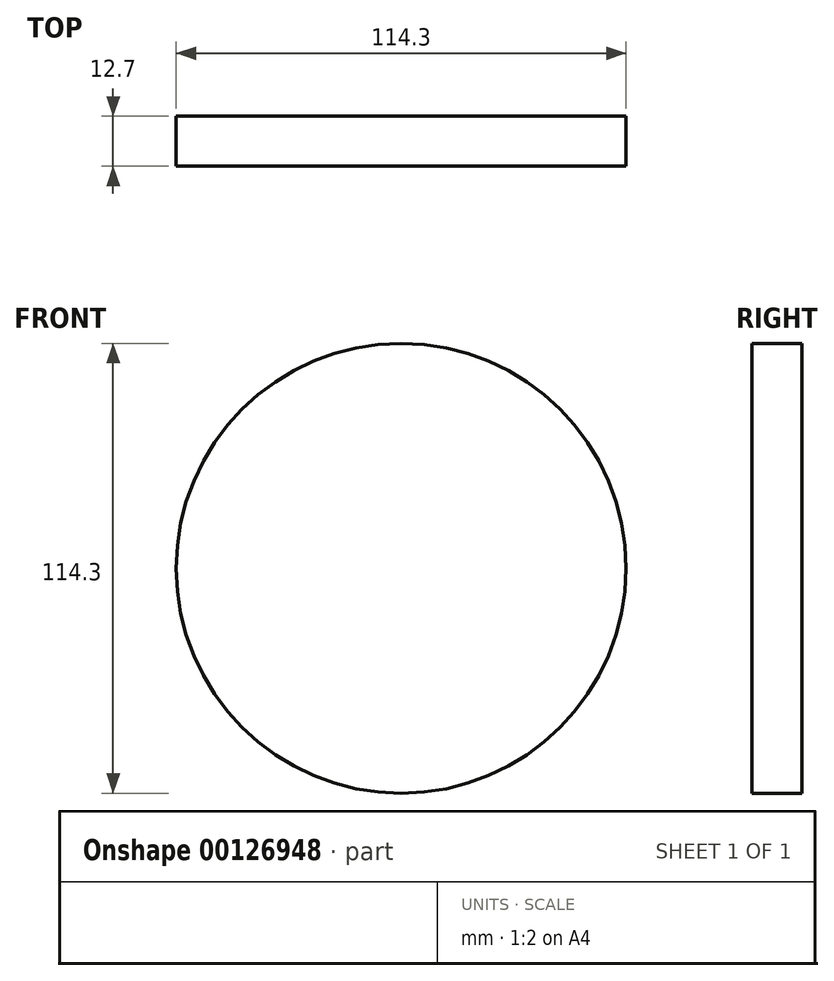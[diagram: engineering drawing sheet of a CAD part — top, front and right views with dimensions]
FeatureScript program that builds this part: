
annotation { "Feature Type Name" : "Feature", "Feature Type Description" : "" }
export const myFeature = defineFeature(function(context is Context, id is Id, definition is map)
    precondition{}
    {
        {
            var Q0;
            Q0=qCreatedBy(makeId("Front.planeOp"),FACE);
            var sketch = newSketch(context, id + "F0", { "sketchPlane" : qUnion([Q0])});
            skCircle(sketch, "E0", {"center": v(0, 0) * mm, "radius": 57.15 * mm});
            skSolve(sketch);
        }
        {
            var Q0;
            Q0=makeQuery(id+"F0.imprint","IMPRINT",FACE,{"disambiguationData":[TD([[makeQuery(id+"F0.imprint","IMPRINT",EDGE,{"derivedFrom":sQuery(id+"F0.wireOp",EDGE,"E0")}),1.0]])]});
            extrude(context, id + "F1", {"entities" : qUnion([Q0]), "depth" : 12.7 * mm});
        }
    });
